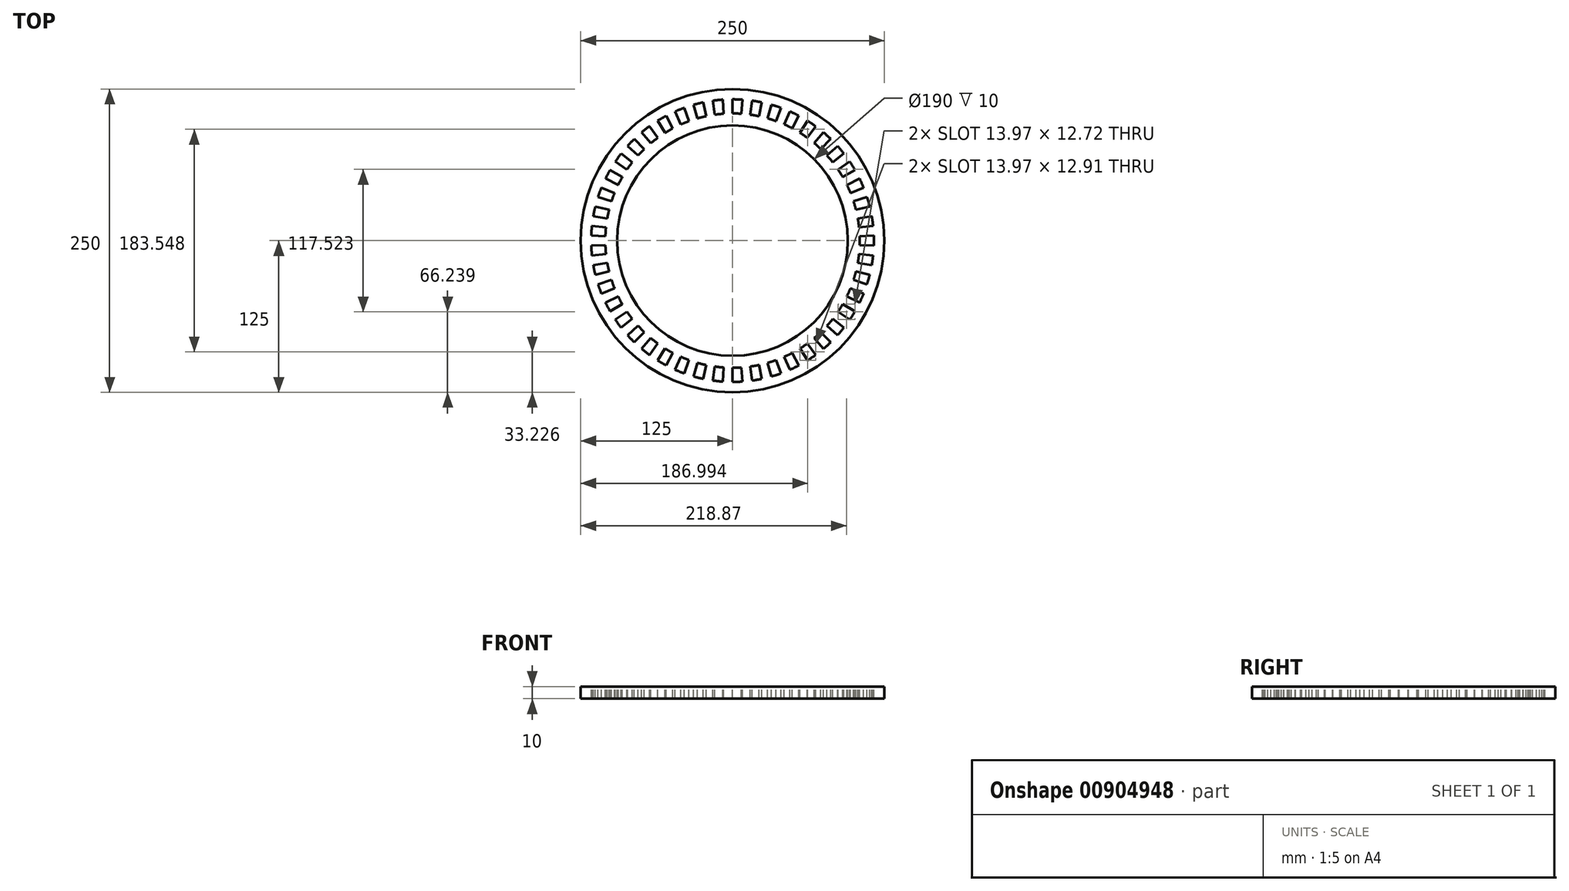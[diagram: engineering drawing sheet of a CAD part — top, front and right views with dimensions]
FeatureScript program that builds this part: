
annotation { "Feature Type Name" : "Feature", "Feature Type Description" : "" }
export const myFeature = defineFeature(function(context is Context, id is Id, definition is map)
    precondition{}
    {
        {
            var Q0;
            Q0=qCreatedBy(makeId("Top.planeOp"),FACE);
            var sketch = newSketch(context, id + "F0", { "sketchPlane" : qUnion([Q0])});
            skCircle(sketch, "E0", {"center": v(0, 0) * mm, "radius": 145 * mm});
            skArc(sketch, "E1", {"start": v(9.54, 136.41) * mm, "mid": v(4.77, 136.66) * mm, "end": v(0, 136.75) * mm});
            skArc(sketch, "E2", {"start": v(8, 114.55) * mm, "mid": v(4, 114.76) * mm, "end": v(0, 114.83) * mm});
            skLineSegment(sketch, "E3", {"start": v(0, 0) * mm, "end": v(0, 38.61) * mm, "construction": true});
            skLineSegment(sketch, "E4", {"start": v(0, 38.61) * mm, "end": v(0, 0) * mm, "construction": true});
            skLineSegment(sketch, "E5", {"start": v(0, 0) * mm, "end": v(-47.77, 0) * mm, "construction": true});
            skLineSegment(sketch, "E6", {"start": v(0, 30) * mm, "end": v(-10, 30) * mm});
            skLineSegment(sketch, "E7", {"start": v(-10, 30) * mm, "end": v(-10, 10) * mm});
            skLineSegment(sketch, "E8", {"start": v(-10, 10) * mm, "end": v(-30, 10) * mm});
            skLineSegment(sketch, "E9", {"start": v(-30, 10) * mm, "end": v(-30, 0) * mm});
            skLineSegment(sketch, "E10.MirrorCS", {"start": v(-30, -10) * mm, "end": v(-30, 0) * mm});
            skLineSegment(sketch, "E11.MirrorCS", {"start": v(-10, -10) * mm, "end": v(-30, -10) * mm});
            skLineSegment(sketch, "E12.MirrorCS", {"start": v(-10, -30) * mm, "end": v(-10, -10) * mm});
            skLineSegment(sketch, "E13.MirrorCS", {"start": v(0, -30) * mm, "end": v(-10, -30) * mm});
            skLineSegment(sketch, "E14.MirrorCS", {"start": v(0, 30) * mm, "end": v(10, 30) * mm});
            skLineSegment(sketch, "E15.MirrorCS", {"start": v(10, 30) * mm, "end": v(10, 10) * mm});
            skLineSegment(sketch, "E16.MirrorCS", {"start": v(10, 10) * mm, "end": v(30, 10) * mm});
            skLineSegment(sketch, "E17.MirrorCS", {"start": v(30, 10) * mm, "end": v(30, 0) * mm});
            skLineSegment(sketch, "E18.MirrorCS", {"start": v(30, -10) * mm, "end": v(30, 0) * mm});
            skLineSegment(sketch, "E19.MirrorCS", {"start": v(10, -10) * mm, "end": v(30, -10) * mm});
            skLineSegment(sketch, "E20.MirrorCS", {"start": v(0, -30) * mm, "end": v(10, -30) * mm});
            skLineSegment(sketch, "E21.MirrorCS", {"start": v(10, -30) * mm, "end": v(10, -10) * mm});
            skLineSegment(sketch, "E22", {"start": v(0, 114.83) * mm, "end": v(0, 136.75) * mm});
            skLineSegment(sketch, "E23", {"start": v(8, 114.55) * mm, "end": v(9.54, 136.41) * mm});
            skArc(sketch, "E24.1.0", {"start": v(-10, 114.4) * mm, "mid": v(-14, 113.98) * mm, "end": v(-17.96, 113.42) * mm});
            skLineSegment(sketch, "E24.1.1", {"start": v(-17.96, 113.42) * mm, "end": v(-21.4, 135.06) * mm});
            skArc(sketch, "E24.1.2", {"start": v(-11.92, 136.23) * mm, "mid": v(-16.67, 135.73) * mm, "end": v(-21.4, 135.06) * mm});
            skLineSegment(sketch, "E24.1.3", {"start": v(-10, 114.4) * mm, "end": v(-11.92, 136.23) * mm});
            skArc(sketch, "E24.2.0", {"start": v(-27.78, 111.42) * mm, "mid": v(-31.65, 110.39) * mm, "end": v(-35.49, 109.21) * mm});
            skLineSegment(sketch, "E24.2.1", {"start": v(-35.49, 109.21) * mm, "end": v(-42.26, 130.05) * mm});
            skArc(sketch, "E24.2.2", {"start": v(-33.08, 132.68) * mm, "mid": v(-37.7, 131.45) * mm, "end": v(-42.26, 130.05) * mm});
            skLineSegment(sketch, "E24.2.3", {"start": v(-27.78, 111.42) * mm, "end": v(-33.08, 132.68) * mm});
            skArc(sketch, "E24.3.0", {"start": v(-44.87, 105.7) * mm, "mid": v(-48.53, 104.07) * mm, "end": v(-52.13, 102.32) * mm});
            skLineSegment(sketch, "E24.3.1", {"start": v(-52.13, 102.32) * mm, "end": v(-62.08, 121.84) * mm});
            skArc(sketch, "E24.3.2", {"start": v(-53.43, 125.88) * mm, "mid": v(-57.8, 123.93) * mm, "end": v(-62.08, 121.84) * mm});
            skLineSegment(sketch, "E24.3.3", {"start": v(-44.87, 105.7) * mm, "end": v(-53.43, 125.88) * mm});
            skArc(sketch, "E24.4.0", {"start": v(-60.85, 97.38) * mm, "mid": v(-64.21, 95.2) * mm, "end": v(-67.5, 92.9) * mm});
            skLineSegment(sketch, "E24.4.1", {"start": v(-67.5, 92.9) * mm, "end": v(-80.38, 110.63) * mm});
            skArc(sketch, "E24.4.2", {"start": v(-72.47, 115.97) * mm, "mid": v(-76.47, 113.37) * mm, "end": v(-80.38, 110.63) * mm});
            skLineSegment(sketch, "E24.4.3", {"start": v(-60.85, 97.38) * mm, "end": v(-72.47, 115.97) * mm});
            skArc(sketch, "E24.5.0", {"start": v(-75.34, 86.67) * mm, "mid": v(-78.32, 83.98) * mm, "end": v(-81.2, 81.2) * mm});
            skLineSegment(sketch, "E24.5.1", {"start": v(-81.2, 81.2) * mm, "end": v(-96.7, 96.7) * mm});
            skArc(sketch, "E24.5.2", {"start": v(-89.71, 103.2) * mm, "mid": v(-93.26, 100.01) * mm, "end": v(-96.7, 96.7) * mm});
            skLineSegment(sketch, "E24.5.3", {"start": v(-75.34, 86.67) * mm, "end": v(-89.71, 103.2) * mm});
            skArc(sketch, "E24.6.0", {"start": v(-87.97, 73.81) * mm, "mid": v(-90.5, 70.7) * mm, "end": v(-92.9, 67.5) * mm});
            skLineSegment(sketch, "E24.6.1", {"start": v(-92.9, 67.5) * mm, "end": v(-110.63, 80.38) * mm});
            skArc(sketch, "E24.6.2", {"start": v(-104.75, 87.9) * mm, "mid": v(-107.76, 84.19) * mm, "end": v(-110.63, 80.38) * mm});
            skLineSegment(sketch, "E24.6.3", {"start": v(-87.97, 73.81) * mm, "end": v(-104.75, 87.9) * mm});
            skArc(sketch, "E24.7.0", {"start": v(-98.43, 59.14) * mm, "mid": v(-100.44, 55.67) * mm, "end": v(-102.32, 52.13) * mm});
            skLineSegment(sketch, "E24.7.1", {"start": v(-102.32, 52.13) * mm, "end": v(-121.84, 62.08) * mm});
            skArc(sketch, "E24.7.2", {"start": v(-117.22, 70.43) * mm, "mid": v(-119.6, 66.3) * mm, "end": v(-121.84, 62.08) * mm});
            skLineSegment(sketch, "E24.7.3", {"start": v(-98.43, 59.14) * mm, "end": v(-117.22, 70.43) * mm});
            skArc(sketch, "E24.8.0", {"start": v(-106.47, 43.02) * mm, "mid": v(-107.9, 39.28) * mm, "end": v(-109.21, 35.49) * mm});
            skLineSegment(sketch, "E24.8.1", {"start": v(-109.21, 35.49) * mm, "end": v(-130.05, 42.26) * mm});
            skArc(sketch, "E24.8.2", {"start": v(-126.79, 51.23) * mm, "mid": v(-128.5, 46.77) * mm, "end": v(-130.05, 42.26) * mm});
            skLineSegment(sketch, "E24.8.3", {"start": v(-106.47, 43.02) * mm, "end": v(-126.79, 51.23) * mm});
            skArc(sketch, "E24.9.0", {"start": v(-111.9, 25.83) * mm, "mid": v(-112.72, 21.91) * mm, "end": v(-113.42, 17.96) * mm});
            skLineSegment(sketch, "E24.9.1", {"start": v(-113.42, 17.96) * mm, "end": v(-135.06, 21.4) * mm});
            skArc(sketch, "E24.9.2", {"start": v(-133.24, 30.76) * mm, "mid": v(-134.23, 26.1) * mm, "end": v(-135.06, 21.4) * mm});
            skLineSegment(sketch, "E24.9.3", {"start": v(-111.9, 25.83) * mm, "end": v(-133.24, 30.76) * mm});
            skArc(sketch, "E24.10.0", {"start": v(-114.55, 8) * mm, "mid": v(-114.76, 4) * mm, "end": v(-114.83, 0) * mm});
            skLineSegment(sketch, "E24.10.1", {"start": v(-114.83, 0) * mm, "end": v(-136.75, 0) * mm});
            skArc(sketch, "E24.10.2", {"start": v(-136.41, 9.54) * mm, "mid": v(-136.66, 4.77) * mm, "end": v(-136.75, 0) * mm});
            skLineSegment(sketch, "E24.10.3", {"start": v(-114.55, 8) * mm, "end": v(-136.41, 9.54) * mm});
            skArc(sketch, "E24.11.0", {"start": v(-114.4, -10) * mm, "mid": v(-113.98, -14) * mm, "end": v(-113.42, -17.96) * mm});
            skLineSegment(sketch, "E24.11.1", {"start": v(-113.42, -17.96) * mm, "end": v(-135.06, -21.4) * mm});
            skArc(sketch, "E24.11.2", {"start": v(-136.23, -11.92) * mm, "mid": v(-135.73, -16.67) * mm, "end": v(-135.06, -21.4) * mm});
            skLineSegment(sketch, "E24.11.3", {"start": v(-114.4, -10) * mm, "end": v(-136.23, -11.92) * mm});
            skArc(sketch, "E24.12.0", {"start": v(-111.42, -27.78) * mm, "mid": v(-110.39, -31.65) * mm, "end": v(-109.21, -35.49) * mm});
            skLineSegment(sketch, "E24.12.1", {"start": v(-109.21, -35.49) * mm, "end": v(-130.05, -42.26) * mm});
            skArc(sketch, "E24.12.2", {"start": v(-132.68, -33.08) * mm, "mid": v(-131.45, -37.7) * mm, "end": v(-130.05, -42.26) * mm});
            skLineSegment(sketch, "E24.12.3", {"start": v(-111.42, -27.78) * mm, "end": v(-132.68, -33.08) * mm});
            skArc(sketch, "E24.13.0", {"start": v(-105.7, -44.87) * mm, "mid": v(-104.07, -48.53) * mm, "end": v(-102.32, -52.13) * mm});
            skLineSegment(sketch, "E24.13.1", {"start": v(-102.32, -52.13) * mm, "end": v(-121.84, -62.08) * mm});
            skArc(sketch, "E24.13.2", {"start": v(-125.88, -53.43) * mm, "mid": v(-123.93, -57.8) * mm, "end": v(-121.84, -62.08) * mm});
            skLineSegment(sketch, "E24.13.3", {"start": v(-105.7, -44.87) * mm, "end": v(-125.88, -53.43) * mm});
            skArc(sketch, "E24.14.0", {"start": v(-97.38, -60.85) * mm, "mid": v(-95.2, -64.21) * mm, "end": v(-92.9, -67.5) * mm});
            skLineSegment(sketch, "E24.14.1", {"start": v(-92.9, -67.5) * mm, "end": v(-110.63, -80.38) * mm});
            skArc(sketch, "E24.14.2", {"start": v(-115.97, -72.47) * mm, "mid": v(-113.37, -76.47) * mm, "end": v(-110.63, -80.38) * mm});
            skLineSegment(sketch, "E24.14.3", {"start": v(-97.38, -60.85) * mm, "end": v(-115.97, -72.47) * mm});
            skArc(sketch, "E24.15.0", {"start": v(-86.67, -75.34) * mm, "mid": v(-83.98, -78.32) * mm, "end": v(-81.2, -81.2) * mm});
            skLineSegment(sketch, "E24.15.1", {"start": v(-81.2, -81.2) * mm, "end": v(-96.7, -96.7) * mm});
            skArc(sketch, "E24.15.2", {"start": v(-103.2, -89.71) * mm, "mid": v(-100.01, -93.26) * mm, "end": v(-96.7, -96.7) * mm});
            skLineSegment(sketch, "E24.15.3", {"start": v(-86.67, -75.34) * mm, "end": v(-103.2, -89.71) * mm});
            skArc(sketch, "E24.16.0", {"start": v(-73.81, -87.97) * mm, "mid": v(-70.7, -90.5) * mm, "end": v(-67.5, -92.9) * mm});
            skLineSegment(sketch, "E24.16.1", {"start": v(-67.5, -92.9) * mm, "end": v(-80.38, -110.63) * mm});
            skArc(sketch, "E24.16.2", {"start": v(-87.9, -104.75) * mm, "mid": v(-84.19, -107.76) * mm, "end": v(-80.38, -110.63) * mm});
            skLineSegment(sketch, "E24.16.3", {"start": v(-73.81, -87.97) * mm, "end": v(-87.9, -104.75) * mm});
            skArc(sketch, "E24.17.0", {"start": v(-59.14, -98.43) * mm, "mid": v(-55.67, -100.44) * mm, "end": v(-52.13, -102.32) * mm});
            skLineSegment(sketch, "E24.17.1", {"start": v(-52.13, -102.32) * mm, "end": v(-62.08, -121.84) * mm});
            skArc(sketch, "E24.17.2", {"start": v(-70.43, -117.22) * mm, "mid": v(-66.3, -119.6) * mm, "end": v(-62.08, -121.84) * mm});
            skLineSegment(sketch, "E24.17.3", {"start": v(-59.14, -98.43) * mm, "end": v(-70.43, -117.22) * mm});
            skArc(sketch, "E24.18.0", {"start": v(-43.02, -106.47) * mm, "mid": v(-39.28, -107.9) * mm, "end": v(-35.49, -109.21) * mm});
            skLineSegment(sketch, "E24.18.1", {"start": v(-35.49, -109.21) * mm, "end": v(-42.26, -130.05) * mm});
            skArc(sketch, "E24.18.2", {"start": v(-51.23, -126.79) * mm, "mid": v(-46.77, -128.5) * mm, "end": v(-42.26, -130.05) * mm});
            skLineSegment(sketch, "E24.18.3", {"start": v(-43.02, -106.47) * mm, "end": v(-51.23, -126.79) * mm});
            skArc(sketch, "E24.19.0", {"start": v(-25.83, -111.9) * mm, "mid": v(-21.91, -112.72) * mm, "end": v(-17.96, -113.42) * mm});
            skLineSegment(sketch, "E24.19.1", {"start": v(-17.96, -113.42) * mm, "end": v(-21.4, -135.06) * mm});
            skArc(sketch, "E24.19.2", {"start": v(-30.76, -133.24) * mm, "mid": v(-26.1, -134.23) * mm, "end": v(-21.4, -135.06) * mm});
            skLineSegment(sketch, "E24.19.3", {"start": v(-25.83, -111.9) * mm, "end": v(-30.76, -133.24) * mm});
            skArc(sketch, "E24.20.0", {"start": v(-8, -114.55) * mm, "mid": v(-4, -114.76) * mm, "end": v(0, -114.83) * mm});
            skLineSegment(sketch, "E24.20.1", {"start": v(0, -114.83) * mm, "end": v(0, -136.75) * mm});
            skArc(sketch, "E24.20.2", {"start": v(-9.54, -136.41) * mm, "mid": v(-4.77, -136.66) * mm, "end": v(0, -136.75) * mm});
            skLineSegment(sketch, "E24.20.3", {"start": v(-8, -114.55) * mm, "end": v(-9.54, -136.41) * mm});
            skArc(sketch, "E24.21.0", {"start": v(10, -114.4) * mm, "mid": v(14, -113.98) * mm, "end": v(17.96, -113.42) * mm});
            skLineSegment(sketch, "E24.21.1", {"start": v(17.96, -113.42) * mm, "end": v(21.4, -135.06) * mm});
            skArc(sketch, "E24.21.2", {"start": v(11.92, -136.23) * mm, "mid": v(16.67, -135.73) * mm, "end": v(21.4, -135.06) * mm});
            skLineSegment(sketch, "E24.21.3", {"start": v(10, -114.4) * mm, "end": v(11.92, -136.23) * mm});
            skArc(sketch, "E24.22.0", {"start": v(27.78, -111.42) * mm, "mid": v(31.65, -110.39) * mm, "end": v(35.49, -109.21) * mm});
            skLineSegment(sketch, "E24.22.1", {"start": v(35.49, -109.21) * mm, "end": v(42.26, -130.05) * mm});
            skArc(sketch, "E24.22.2", {"start": v(33.08, -132.68) * mm, "mid": v(37.7, -131.45) * mm, "end": v(42.26, -130.05) * mm});
            skLineSegment(sketch, "E24.22.3", {"start": v(27.78, -111.42) * mm, "end": v(33.08, -132.68) * mm});
            skArc(sketch, "E24.23.0", {"start": v(44.87, -105.7) * mm, "mid": v(48.53, -104.07) * mm, "end": v(52.13, -102.32) * mm});
            skLineSegment(sketch, "E24.23.1", {"start": v(52.13, -102.32) * mm, "end": v(62.08, -121.84) * mm});
            skArc(sketch, "E24.23.2", {"start": v(53.43, -125.88) * mm, "mid": v(57.8, -123.93) * mm, "end": v(62.08, -121.84) * mm});
            skLineSegment(sketch, "E24.23.3", {"start": v(44.87, -105.7) * mm, "end": v(53.43, -125.88) * mm});
            skArc(sketch, "E24.24.0", {"start": v(60.85, -97.38) * mm, "mid": v(64.21, -95.2) * mm, "end": v(67.5, -92.9) * mm});
            skLineSegment(sketch, "E24.24.1", {"start": v(67.5, -92.9) * mm, "end": v(80.38, -110.63) * mm});
            skArc(sketch, "E24.24.2", {"start": v(72.47, -115.97) * mm, "mid": v(76.47, -113.37) * mm, "end": v(80.38, -110.63) * mm});
            skLineSegment(sketch, "E24.24.3", {"start": v(60.85, -97.38) * mm, "end": v(72.47, -115.97) * mm});
            skArc(sketch, "E24.25.0", {"start": v(75.34, -86.67) * mm, "mid": v(78.32, -83.98) * mm, "end": v(81.2, -81.2) * mm});
            skLineSegment(sketch, "E24.25.1", {"start": v(81.2, -81.2) * mm, "end": v(96.7, -96.7) * mm});
            skArc(sketch, "E24.25.2", {"start": v(89.71, -103.2) * mm, "mid": v(93.26, -100.01) * mm, "end": v(96.7, -96.7) * mm});
            skLineSegment(sketch, "E24.25.3", {"start": v(75.34, -86.67) * mm, "end": v(89.71, -103.2) * mm});
            skArc(sketch, "E24.26.0", {"start": v(87.97, -73.81) * mm, "mid": v(90.5, -70.7) * mm, "end": v(92.9, -67.5) * mm});
            skLineSegment(sketch, "E24.26.1", {"start": v(92.9, -67.5) * mm, "end": v(110.63, -80.38) * mm});
            skArc(sketch, "E24.26.2", {"start": v(104.75, -87.9) * mm, "mid": v(107.76, -84.19) * mm, "end": v(110.63, -80.38) * mm});
            skLineSegment(sketch, "E24.26.3", {"start": v(87.97, -73.81) * mm, "end": v(104.75, -87.9) * mm});
            skArc(sketch, "E24.27.0", {"start": v(98.43, -59.14) * mm, "mid": v(100.44, -55.67) * mm, "end": v(102.32, -52.13) * mm});
            skLineSegment(sketch, "E24.27.1", {"start": v(102.32, -52.13) * mm, "end": v(121.84, -62.08) * mm});
            skArc(sketch, "E24.27.2", {"start": v(117.22, -70.43) * mm, "mid": v(119.6, -66.3) * mm, "end": v(121.84, -62.08) * mm});
            skLineSegment(sketch, "E24.27.3", {"start": v(98.43, -59.14) * mm, "end": v(117.22, -70.43) * mm});
            skArc(sketch, "E24.28.0", {"start": v(106.47, -43.02) * mm, "mid": v(107.9, -39.28) * mm, "end": v(109.21, -35.49) * mm});
            skLineSegment(sketch, "E24.28.1", {"start": v(109.21, -35.49) * mm, "end": v(130.05, -42.26) * mm});
            skArc(sketch, "E24.28.2", {"start": v(126.79, -51.23) * mm, "mid": v(128.5, -46.77) * mm, "end": v(130.05, -42.26) * mm});
            skLineSegment(sketch, "E24.28.3", {"start": v(106.47, -43.02) * mm, "end": v(126.79, -51.23) * mm});
            skArc(sketch, "E24.29.0", {"start": v(111.9, -25.83) * mm, "mid": v(112.72, -21.91) * mm, "end": v(113.42, -17.96) * mm});
            skLineSegment(sketch, "E24.29.1", {"start": v(113.42, -17.96) * mm, "end": v(135.06, -21.4) * mm});
            skArc(sketch, "E24.29.2", {"start": v(133.24, -30.76) * mm, "mid": v(134.23, -26.1) * mm, "end": v(135.06, -21.4) * mm});
            skLineSegment(sketch, "E24.29.3", {"start": v(111.9, -25.83) * mm, "end": v(133.24, -30.76) * mm});
            skArc(sketch, "E24.30.0", {"start": v(114.55, -8) * mm, "mid": v(114.76, -4) * mm, "end": v(114.83, 0) * mm});
            skLineSegment(sketch, "E24.30.1", {"start": v(114.83, 0) * mm, "end": v(136.75, 0) * mm});
            skArc(sketch, "E24.30.2", {"start": v(136.41, -9.54) * mm, "mid": v(136.66, -4.77) * mm, "end": v(136.75, 0) * mm});
            skLineSegment(sketch, "E24.30.3", {"start": v(114.55, -8) * mm, "end": v(136.41, -9.54) * mm});
            skArc(sketch, "E24.31.0", {"start": v(114.4, 10) * mm, "mid": v(113.98, 14) * mm, "end": v(113.42, 17.96) * mm});
            skLineSegment(sketch, "E24.31.1", {"start": v(113.42, 17.96) * mm, "end": v(135.06, 21.4) * mm});
            skArc(sketch, "E24.31.2", {"start": v(136.23, 11.92) * mm, "mid": v(135.73, 16.67) * mm, "end": v(135.06, 21.4) * mm});
            skLineSegment(sketch, "E24.31.3", {"start": v(114.4, 10) * mm, "end": v(136.23, 11.92) * mm});
            skArc(sketch, "E24.32.0", {"start": v(111.42, 27.78) * mm, "mid": v(110.39, 31.65) * mm, "end": v(109.21, 35.49) * mm});
            skLineSegment(sketch, "E24.32.1", {"start": v(109.21, 35.49) * mm, "end": v(130.05, 42.26) * mm});
            skArc(sketch, "E24.32.2", {"start": v(132.68, 33.08) * mm, "mid": v(131.45, 37.7) * mm, "end": v(130.05, 42.26) * mm});
            skLineSegment(sketch, "E24.32.3", {"start": v(111.42, 27.78) * mm, "end": v(132.68, 33.08) * mm});
            skArc(sketch, "E24.33.0", {"start": v(105.7, 44.87) * mm, "mid": v(104.07, 48.53) * mm, "end": v(102.32, 52.13) * mm});
            skLineSegment(sketch, "E24.33.1", {"start": v(102.32, 52.13) * mm, "end": v(121.84, 62.08) * mm});
            skArc(sketch, "E24.33.2", {"start": v(125.88, 53.43) * mm, "mid": v(123.93, 57.8) * mm, "end": v(121.84, 62.08) * mm});
            skLineSegment(sketch, "E24.33.3", {"start": v(105.7, 44.87) * mm, "end": v(125.88, 53.43) * mm});
            skArc(sketch, "E24.34.0", {"start": v(97.38, 60.85) * mm, "mid": v(95.2, 64.21) * mm, "end": v(92.9, 67.5) * mm});
            skLineSegment(sketch, "E24.34.1", {"start": v(92.9, 67.5) * mm, "end": v(110.63, 80.38) * mm});
            skArc(sketch, "E24.34.2", {"start": v(115.97, 72.47) * mm, "mid": v(113.37, 76.47) * mm, "end": v(110.63, 80.38) * mm});
            skLineSegment(sketch, "E24.34.3", {"start": v(97.38, 60.85) * mm, "end": v(115.97, 72.47) * mm});
            skArc(sketch, "E24.35.0", {"start": v(86.67, 75.34) * mm, "mid": v(83.98, 78.32) * mm, "end": v(81.2, 81.2) * mm});
            skLineSegment(sketch, "E24.35.1", {"start": v(81.2, 81.2) * mm, "end": v(96.7, 96.7) * mm});
            skArc(sketch, "E24.35.2", {"start": v(103.2, 89.71) * mm, "mid": v(100.01, 93.26) * mm, "end": v(96.7, 96.7) * mm});
            skLineSegment(sketch, "E24.35.3", {"start": v(86.67, 75.34) * mm, "end": v(103.2, 89.71) * mm});
            skArc(sketch, "E24.36.0", {"start": v(73.81, 87.97) * mm, "mid": v(70.7, 90.5) * mm, "end": v(67.5, 92.9) * mm});
            skLineSegment(sketch, "E24.36.1", {"start": v(67.5, 92.9) * mm, "end": v(80.38, 110.63) * mm});
            skArc(sketch, "E24.36.2", {"start": v(87.9, 104.75) * mm, "mid": v(84.19, 107.76) * mm, "end": v(80.38, 110.63) * mm});
            skLineSegment(sketch, "E24.36.3", {"start": v(73.81, 87.97) * mm, "end": v(87.9, 104.75) * mm});
            skArc(sketch, "E24.37.0", {"start": v(59.14, 98.43) * mm, "mid": v(55.67, 100.44) * mm, "end": v(52.13, 102.32) * mm});
            skLineSegment(sketch, "E24.37.1", {"start": v(52.13, 102.32) * mm, "end": v(62.08, 121.84) * mm});
            skArc(sketch, "E24.37.2", {"start": v(70.43, 117.22) * mm, "mid": v(66.3, 119.6) * mm, "end": v(62.08, 121.84) * mm});
            skLineSegment(sketch, "E24.37.3", {"start": v(59.14, 98.43) * mm, "end": v(70.43, 117.22) * mm});
            skArc(sketch, "E24.38.0", {"start": v(43.02, 106.47) * mm, "mid": v(39.28, 107.9) * mm, "end": v(35.49, 109.21) * mm});
            skLineSegment(sketch, "E24.38.1", {"start": v(35.49, 109.21) * mm, "end": v(42.26, 130.05) * mm});
            skArc(sketch, "E24.38.2", {"start": v(51.23, 126.79) * mm, "mid": v(46.77, 128.5) * mm, "end": v(42.26, 130.05) * mm});
            skLineSegment(sketch, "E24.38.3", {"start": v(43.02, 106.47) * mm, "end": v(51.23, 126.79) * mm});
            skArc(sketch, "E24.39.0", {"start": v(25.83, 111.9) * mm, "mid": v(21.91, 112.72) * mm, "end": v(17.96, 113.42) * mm});
            skLineSegment(sketch, "E24.39.1", {"start": v(17.96, 113.42) * mm, "end": v(21.4, 135.06) * mm});
            skArc(sketch, "E24.39.2", {"start": v(30.76, 133.24) * mm, "mid": v(26.1, 134.23) * mm, "end": v(21.4, 135.06) * mm});
            skLineSegment(sketch, "E24.39.3", {"start": v(25.83, 111.9) * mm, "end": v(30.76, 133.24) * mm});
            skCircle(sketch, "E25", {"center": v(0, 0) * mm, "radius": 50 * mm});
            skSolve(sketch);
        }
        {
            var Q0;
            Q0=makeQuery(id+"F0.imprint","IMPRINT",FACE,{"disambiguationData":[TD([[makeQuery(id+"F0.imprint","IMPRINT",EDGE,{"derivedFrom":sQuery(id+"F0.wireOp",EDGE,"E6")}),-1.0]])]});
            extrude(context, id + "F1", {"entities" : qUnion([Q0]), "depth" : 5 * mm, "offsetDistance" : 25 * mm});
        }
        {
            var Q0;
            Q0=makeQuery(id+"F1.opExtrude","CAP_FACE",FACE,{"disambiguationData":[OSD([sQuery(id+"F0.wireOp",EDGE,"E6"),sQuery(id+"F0.wireOp",EDGE,"E7"),sQuery(id+"F0.wireOp",EDGE,"E8"),sQuery(id+"F0.wireOp",EDGE,"E9"),sQuery(id+"F0.wireOp",EDGE,"E10.MirrorCS"),sQuery(id+"F0.wireOp",EDGE,"E11.MirrorCS"),sQuery(id+"F0.wireOp",EDGE,"E12.MirrorCS"),sQuery(id+"F0.wireOp",EDGE,"E13.MirrorCS"),sQuery(id+"F0.wireOp",EDGE,"E14.MirrorCS"),sQuery(id+"F0.wireOp",EDGE,"E15.MirrorCS"),sQuery(id+"F0.wireOp",EDGE,"E16.MirrorCS"),sQuery(id+"F0.wireOp",EDGE,"E17.MirrorCS"),sQuery(id+"F0.wireOp",EDGE,"E18.MirrorCS"),sQuery(id+"F0.wireOp",EDGE,"E19.MirrorCS"),sQuery(id+"F0.wireOp",EDGE,"E20.MirrorCS"),sQuery(id+"F0.wireOp",EDGE,"E21.MirrorCS"),sQuery(id+"F0.wireOp",EDGE,"E25")])],"isStart":false});
            var sketch = newSketch(context, id + "F2", { "sketchPlane" : qUnion([Q0])});
            skCircle(sketch, "E26", {"center": v(0, 0) * mm, "radius": 125 * mm});
            skCircle(sketch, "E27", {"center": v(0, 0) * mm, "radius": 40.45 * mm});
            skSolve(sketch);
        }
        {
            var Q0;
            Q0=qSketchRegion(id+"F2",true);
            extrude(context, id + "F3", {"entities" : qUnion([Q0]), "operationType" : NewBodyOperationType.ADD, "oppositeDirection" : true, "depth" : 10 * mm, "offsetDistance" : 25 * mm});
        }
        {
            var Q0;
            Q0=makeQuery(id+"F3.boolean.opBoolean","MERGE",FACE,{"derivedFrom":[makeQuery(id+"F1.opExtrude","CAP_FACE",FACE,{"disambiguationData":[OSD([sQuery(id+"F0.wireOp",EDGE,"E6"),sQuery(id+"F0.wireOp",EDGE,"E7"),sQuery(id+"F0.wireOp",EDGE,"E8"),sQuery(id+"F0.wireOp",EDGE,"E9"),sQuery(id+"F0.wireOp",EDGE,"E10.MirrorCS"),sQuery(id+"F0.wireOp",EDGE,"E11.MirrorCS"),sQuery(id+"F0.wireOp",EDGE,"E12.MirrorCS"),sQuery(id+"F0.wireOp",EDGE,"E13.MirrorCS"),sQuery(id+"F0.wireOp",EDGE,"E14.MirrorCS"),sQuery(id+"F0.wireOp",EDGE,"E15.MirrorCS"),sQuery(id+"F0.wireOp",EDGE,"E16.MirrorCS"),sQuery(id+"F0.wireOp",EDGE,"E17.MirrorCS"),sQuery(id+"F0.wireOp",EDGE,"E18.MirrorCS"),sQuery(id+"F0.wireOp",EDGE,"E19.MirrorCS"),sQuery(id+"F0.wireOp",EDGE,"E20.MirrorCS"),sQuery(id+"F0.wireOp",EDGE,"E21.MirrorCS"),sQuery(id+"F0.wireOp",EDGE,"E25")])],"isStart":false}),makeQuery(id+"F3.opExtrude","CAP_FACE",FACE,{"disambiguationData":[OSD([sQuery(id+"F2.wireOp",EDGE,"E26"),sQuery(id+"F2.wireOp",EDGE,"E27")])],"isStart":true})]});
            var sketch = newSketch(context, id + "F4", { "sketchPlane" : qUnion([Q0])});
            skLineSegment(sketch, "E28", {"start": v(0, 104.8) * mm, "end": v(0, 116.46) * mm});
            skLineSegment(sketch, "E29", {"start": v(0, 116.46) * mm, "end": v(0, 104.8) * mm});
            skLineSegment(sketch, "E30", {"start": v(7.31, 104.55) * mm, "end": v(8.12, 116.17) * mm});
            skArc(sketch, "E31", {"start": v(8.12, 116.17) * mm, "mid": v(4.06, 116.39) * mm, "end": v(0, 116.46) * mm});
            skArc(sketch, "E32", {"start": v(7.31, 104.55) * mm, "mid": v(3.66, 104.74) * mm, "end": v(0, 104.8) * mm});
            skArc(sketch, "E33.1.0", {"start": v(-7.31, 104.55) * mm, "mid": v(-10.95, 104.23) * mm, "end": v(-14.59, 103.78) * mm});
            skLineSegment(sketch, "E33.1.1", {"start": v(-16.2, 115.32) * mm, "end": v(-14.59, 103.78) * mm});
            skArc(sketch, "E33.1.2", {"start": v(-8.12, 116.17) * mm, "mid": v(-12.17, 115.82) * mm, "end": v(-16.2, 115.32) * mm});
            skLineSegment(sketch, "E33.1.3", {"start": v(-7.31, 104.55) * mm, "end": v(-8.12, 116.17) * mm});
            skArc(sketch, "E33.2.0", {"start": v(-21.79, 102.51) * mm, "mid": v(-25.35, 101.69) * mm, "end": v(-28.89, 100.74) * mm});
            skLineSegment(sketch, "E33.2.1", {"start": v(-32.1, 111.95) * mm, "end": v(-28.89, 100.74) * mm});
            skArc(sketch, "E33.2.2", {"start": v(-24.21, 113.91) * mm, "mid": v(-28.17, 113) * mm, "end": v(-32.1, 111.95) * mm});
            skLineSegment(sketch, "E33.2.3", {"start": v(-21.79, 102.51) * mm, "end": v(-24.21, 113.91) * mm});
            skArc(sketch, "E33.3.0", {"start": v(-35.84, 98.48) * mm, "mid": v(-39.26, 97.17) * mm, "end": v(-42.63, 95.74) * mm});
            skLineSegment(sketch, "E33.3.1", {"start": v(-47.37, 106.39) * mm, "end": v(-42.63, 95.74) * mm});
            skArc(sketch, "E33.3.2", {"start": v(-39.83, 109.43) * mm, "mid": v(-43.63, 107.98) * mm, "end": v(-47.37, 106.39) * mm});
            skLineSegment(sketch, "E33.3.3", {"start": v(-35.84, 98.48) * mm, "end": v(-39.83, 109.43) * mm});
            skArc(sketch, "E33.4.0", {"start": v(-49.2, 92.54) * mm, "mid": v(-52.4, 90.76) * mm, "end": v(-55.54, 88.88) * mm});
            skLineSegment(sketch, "E33.4.1", {"start": v(-61.71, 98.76) * mm, "end": v(-55.54, 88.88) * mm});
            skArc(sketch, "E33.4.2", {"start": v(-54.67, 102.82) * mm, "mid": v(-58.23, 100.85) * mm, "end": v(-61.71, 98.76) * mm});
            skLineSegment(sketch, "E33.4.3", {"start": v(-49.2, 92.54) * mm, "end": v(-54.67, 102.82) * mm});
            skArc(sketch, "E33.5.0", {"start": v(-61.6, 84.79) * mm, "mid": v(-64.52, 82.59) * mm, "end": v(-67.37, 80.28) * mm});
            skLineSegment(sketch, "E33.5.1", {"start": v(-74.86, 89.21) * mm, "end": v(-67.37, 80.28) * mm});
            skArc(sketch, "E33.5.2", {"start": v(-68.45, 94.22) * mm, "mid": v(-71.7, 91.77) * mm, "end": v(-74.86, 89.21) * mm});
            skLineSegment(sketch, "E33.5.3", {"start": v(-61.6, 84.79) * mm, "end": v(-68.45, 94.22) * mm});
            skArc(sketch, "E33.6.0", {"start": v(-72.8, 75.39) * mm, "mid": v(-75.39, 72.8) * mm, "end": v(-77.88, 70.13) * mm});
            skLineSegment(sketch, "E33.6.1", {"start": v(-86.54, 77.92) * mm, "end": v(-77.88, 70.13) * mm});
            skArc(sketch, "E33.6.2", {"start": v(-80.9, 83.77) * mm, "mid": v(-83.77, 80.9) * mm, "end": v(-86.54, 77.92) * mm});
            skLineSegment(sketch, "E33.6.3", {"start": v(-72.8, 75.39) * mm, "end": v(-80.9, 83.77) * mm});
            skArc(sketch, "E33.7.0", {"start": v(-82.59, 64.52) * mm, "mid": v(-84.79, 61.6) * mm, "end": v(-86.89, 58.6) * mm});
            skLineSegment(sketch, "E33.7.1", {"start": v(-96.55, 65.12) * mm, "end": v(-86.89, 58.6) * mm});
            skArc(sketch, "E33.7.2", {"start": v(-91.77, 71.7) * mm, "mid": v(-94.22, 68.45) * mm, "end": v(-96.55, 65.12) * mm});
            skLineSegment(sketch, "E33.7.3", {"start": v(-82.59, 64.52) * mm, "end": v(-91.77, 71.7) * mm});
            skArc(sketch, "E33.8.0", {"start": v(-90.76, 52.4) * mm, "mid": v(-92.54, 49.2) * mm, "end": v(-94.2, 45.94) * mm});
            skLineSegment(sketch, "E33.8.1", {"start": v(-104.67, 51.05) * mm, "end": v(-94.2, 45.94) * mm});
            skArc(sketch, "E33.8.2", {"start": v(-100.85, 58.23) * mm, "mid": v(-102.82, 54.67) * mm, "end": v(-104.67, 51.05) * mm});
            skLineSegment(sketch, "E33.8.3", {"start": v(-90.76, 52.4) * mm, "end": v(-100.85, 58.23) * mm});
            skArc(sketch, "E33.9.0", {"start": v(-97.17, 39.26) * mm, "mid": v(-98.48, 35.84) * mm, "end": v(-99.67, 32.39) * mm});
            skLineSegment(sketch, "E33.9.1", {"start": v(-110.76, 35.99) * mm, "end": v(-99.67, 32.39) * mm});
            skArc(sketch, "E33.9.2", {"start": v(-107.98, 43.63) * mm, "mid": v(-109.43, 39.83) * mm, "end": v(-110.76, 35.99) * mm});
            skLineSegment(sketch, "E33.9.3", {"start": v(-97.17, 39.26) * mm, "end": v(-107.98, 43.63) * mm});
            skArc(sketch, "E33.10.0", {"start": v(-101.69, 25.35) * mm, "mid": v(-102.51, 21.79) * mm, "end": v(-103.21, 18.2) * mm});
            skLineSegment(sketch, "E33.10.1", {"start": v(-114.69, 20.22) * mm, "end": v(-103.21, 18.2) * mm});
            skArc(sketch, "E33.10.2", {"start": v(-113, 28.17) * mm, "mid": v(-113.91, 24.21) * mm, "end": v(-114.69, 20.22) * mm});
            skLineSegment(sketch, "E33.10.3", {"start": v(-101.69, 25.35) * mm, "end": v(-113, 28.17) * mm});
            skArc(sketch, "E33.11.0", {"start": v(-104.23, 10.95) * mm, "mid": v(-104.55, 7.31) * mm, "end": v(-104.74, 3.66) * mm});
            skLineSegment(sketch, "E33.11.1", {"start": v(-116.39, 4.06) * mm, "end": v(-104.74, 3.66) * mm});
            skArc(sketch, "E33.11.2", {"start": v(-115.82, 12.17) * mm, "mid": v(-116.17, 8.12) * mm, "end": v(-116.39, 4.06) * mm});
            skLineSegment(sketch, "E33.11.3", {"start": v(-104.23, 10.95) * mm, "end": v(-115.82, 12.17) * mm});
            skArc(sketch, "E33.12.0", {"start": v(-104.74, -3.66) * mm, "mid": v(-104.55, -7.31) * mm, "end": v(-104.23, -10.95) * mm});
            skLineSegment(sketch, "E33.12.1", {"start": v(-115.82, -12.17) * mm, "end": v(-104.23, -10.95) * mm});
            skArc(sketch, "E33.12.2", {"start": v(-116.39, -4.06) * mm, "mid": v(-116.17, -8.12) * mm, "end": v(-115.82, -12.17) * mm});
            skLineSegment(sketch, "E33.12.3", {"start": v(-104.74, -3.66) * mm, "end": v(-116.39, -4.06) * mm});
            skArc(sketch, "E33.13.0", {"start": v(-103.21, -18.2) * mm, "mid": v(-102.51, -21.79) * mm, "end": v(-101.69, -25.35) * mm});
            skLineSegment(sketch, "E33.13.1", {"start": v(-113, -28.17) * mm, "end": v(-101.69, -25.35) * mm});
            skArc(sketch, "E33.13.2", {"start": v(-114.69, -20.22) * mm, "mid": v(-113.91, -24.21) * mm, "end": v(-113, -28.17) * mm});
            skLineSegment(sketch, "E33.13.3", {"start": v(-103.21, -18.2) * mm, "end": v(-114.69, -20.22) * mm});
            skArc(sketch, "E33.14.0", {"start": v(-99.67, -32.39) * mm, "mid": v(-98.48, -35.84) * mm, "end": v(-97.17, -39.26) * mm});
            skLineSegment(sketch, "E33.14.1", {"start": v(-107.98, -43.63) * mm, "end": v(-97.17, -39.26) * mm});
            skArc(sketch, "E33.14.2", {"start": v(-110.76, -35.99) * mm, "mid": v(-109.43, -39.83) * mm, "end": v(-107.98, -43.63) * mm});
            skLineSegment(sketch, "E33.14.3", {"start": v(-99.67, -32.39) * mm, "end": v(-110.76, -35.99) * mm});
            skArc(sketch, "E33.15.0", {"start": v(-94.2, -45.94) * mm, "mid": v(-92.54, -49.2) * mm, "end": v(-90.76, -52.4) * mm});
            skLineSegment(sketch, "E33.15.1", {"start": v(-100.85, -58.23) * mm, "end": v(-90.76, -52.4) * mm});
            skArc(sketch, "E33.15.2", {"start": v(-104.67, -51.05) * mm, "mid": v(-102.82, -54.67) * mm, "end": v(-100.85, -58.23) * mm});
            skLineSegment(sketch, "E33.15.3", {"start": v(-94.2, -45.94) * mm, "end": v(-104.67, -51.05) * mm});
            skArc(sketch, "E33.16.0", {"start": v(-86.89, -58.6) * mm, "mid": v(-84.79, -61.6) * mm, "end": v(-82.59, -64.52) * mm});
            skLineSegment(sketch, "E33.16.1", {"start": v(-91.77, -71.7) * mm, "end": v(-82.59, -64.52) * mm});
            skArc(sketch, "E33.16.2", {"start": v(-96.55, -65.12) * mm, "mid": v(-94.22, -68.45) * mm, "end": v(-91.77, -71.7) * mm});
            skLineSegment(sketch, "E33.16.3", {"start": v(-86.89, -58.6) * mm, "end": v(-96.55, -65.12) * mm});
            skArc(sketch, "E33.17.0", {"start": v(-77.88, -70.13) * mm, "mid": v(-75.39, -72.8) * mm, "end": v(-72.8, -75.39) * mm});
            skLineSegment(sketch, "E33.17.1", {"start": v(-80.9, -83.77) * mm, "end": v(-72.8, -75.39) * mm});
            skArc(sketch, "E33.17.2", {"start": v(-86.54, -77.92) * mm, "mid": v(-83.77, -80.9) * mm, "end": v(-80.9, -83.77) * mm});
            skLineSegment(sketch, "E33.17.3", {"start": v(-77.88, -70.13) * mm, "end": v(-86.54, -77.92) * mm});
            skArc(sketch, "E34.3.18.0", {"start": v(-67.37, -80.28) * mm, "mid": v(-64.52, -82.59) * mm, "end": v(-61.6, -84.79) * mm});
            skLineSegment(sketch, "E34.4.18.0", {"start": v(-68.45, -94.22) * mm, "end": v(-61.6, -84.79) * mm});
            skArc(sketch, "E34.7.18.0", {"start": v(-74.86, -89.21) * mm, "mid": v(-71.7, -91.77) * mm, "end": v(-68.45, -94.22) * mm});
            skLineSegment(sketch, "E34.11.18.0", {"start": v(-67.37, -80.28) * mm, "end": v(-74.86, -89.21) * mm});
            skArc(sketch, "E34.3.19.0", {"start": v(-55.54, -88.88) * mm, "mid": v(-52.4, -90.76) * mm, "end": v(-49.2, -92.54) * mm});
            skLineSegment(sketch, "E34.4.19.0", {"start": v(-54.67, -102.82) * mm, "end": v(-49.2, -92.54) * mm});
            skArc(sketch, "E34.7.19.0", {"start": v(-61.71, -98.76) * mm, "mid": v(-58.23, -100.85) * mm, "end": v(-54.67, -102.82) * mm});
            skLineSegment(sketch, "E34.11.19.0", {"start": v(-55.54, -88.88) * mm, "end": v(-61.71, -98.76) * mm});
            skArc(sketch, "E34.3.20.0", {"start": v(-42.63, -95.74) * mm, "mid": v(-39.26, -97.17) * mm, "end": v(-35.84, -98.48) * mm});
            skLineSegment(sketch, "E34.4.20.0", {"start": v(-39.83, -109.43) * mm, "end": v(-35.84, -98.48) * mm});
            skArc(sketch, "E34.7.20.0", {"start": v(-47.37, -106.39) * mm, "mid": v(-43.63, -107.98) * mm, "end": v(-39.83, -109.43) * mm});
            skLineSegment(sketch, "E34.11.20.0", {"start": v(-42.63, -95.74) * mm, "end": v(-47.37, -106.39) * mm});
            skArc(sketch, "E34.3.21.0", {"start": v(-28.89, -100.74) * mm, "mid": v(-25.35, -101.69) * mm, "end": v(-21.79, -102.51) * mm});
            skLineSegment(sketch, "E34.4.21.0", {"start": v(-24.21, -113.91) * mm, "end": v(-21.79, -102.51) * mm});
            skArc(sketch, "E34.7.21.0", {"start": v(-32.1, -111.95) * mm, "mid": v(-28.17, -113) * mm, "end": v(-24.21, -113.91) * mm});
            skLineSegment(sketch, "E34.11.21.0", {"start": v(-28.89, -100.74) * mm, "end": v(-32.1, -111.95) * mm});
            skArc(sketch, "E34.3.22.0", {"start": v(-14.59, -103.78) * mm, "mid": v(-10.95, -104.23) * mm, "end": v(-7.31, -104.55) * mm});
            skLineSegment(sketch, "E34.4.22.0", {"start": v(-8.12, -116.17) * mm, "end": v(-7.31, -104.55) * mm});
            skArc(sketch, "E34.7.22.0", {"start": v(-16.2, -115.32) * mm, "mid": v(-12.17, -115.82) * mm, "end": v(-8.12, -116.17) * mm});
            skLineSegment(sketch, "E34.11.22.0", {"start": v(-14.59, -103.78) * mm, "end": v(-16.2, -115.32) * mm});
            skArc(sketch, "E34.3.23.0", {"start": v(0, -104.8) * mm, "mid": v(3.66, -104.74) * mm, "end": v(7.31, -104.55) * mm});
            skLineSegment(sketch, "E34.4.23.0", {"start": v(8.12, -116.17) * mm, "end": v(7.31, -104.55) * mm});
            skArc(sketch, "E34.7.23.0", {"start": v(0, -116.46) * mm, "mid": v(4.06, -116.39) * mm, "end": v(8.12, -116.17) * mm});
            skLineSegment(sketch, "E34.11.23.0", {"start": v(0, -104.8) * mm, "end": v(0, -116.46) * mm});
            skArc(sketch, "E34.3.24.0", {"start": v(14.59, -103.78) * mm, "mid": v(18.2, -103.21) * mm, "end": v(21.79, -102.51) * mm});
            skLineSegment(sketch, "E34.4.24.0", {"start": v(24.21, -113.91) * mm, "end": v(21.79, -102.51) * mm});
            skArc(sketch, "E34.7.24.0", {"start": v(16.2, -115.32) * mm, "mid": v(20.22, -114.69) * mm, "end": v(24.21, -113.91) * mm});
            skLineSegment(sketch, "E34.11.24.0", {"start": v(14.59, -103.78) * mm, "end": v(16.2, -115.32) * mm});
            skArc(sketch, "E34.3.25.0", {"start": v(28.89, -100.74) * mm, "mid": v(32.39, -99.67) * mm, "end": v(35.84, -98.48) * mm});
            skLineSegment(sketch, "E34.4.25.0", {"start": v(39.83, -109.43) * mm, "end": v(35.84, -98.48) * mm});
            skArc(sketch, "E34.7.25.0", {"start": v(32.1, -111.95) * mm, "mid": v(35.99, -110.76) * mm, "end": v(39.83, -109.43) * mm});
            skLineSegment(sketch, "E34.11.25.0", {"start": v(28.89, -100.74) * mm, "end": v(32.1, -111.95) * mm});
            skArc(sketch, "E34.3.26.0", {"start": v(42.63, -95.74) * mm, "mid": v(45.94, -94.2) * mm, "end": v(49.2, -92.54) * mm});
            skLineSegment(sketch, "E34.4.26.0", {"start": v(54.67, -102.82) * mm, "end": v(49.2, -92.54) * mm});
            skArc(sketch, "E34.7.26.0", {"start": v(47.37, -106.39) * mm, "mid": v(51.05, -104.67) * mm, "end": v(54.67, -102.82) * mm});
            skLineSegment(sketch, "E34.11.26.0", {"start": v(42.63, -95.74) * mm, "end": v(47.37, -106.39) * mm});
            skArc(sketch, "E34.3.27.0", {"start": v(55.54, -88.88) * mm, "mid": v(58.6, -86.89) * mm, "end": v(61.6, -84.79) * mm});
            skLineSegment(sketch, "E34.4.27.0", {"start": v(68.45, -94.22) * mm, "end": v(61.6, -84.79) * mm});
            skArc(sketch, "E34.7.27.0", {"start": v(61.71, -98.76) * mm, "mid": v(65.12, -96.55) * mm, "end": v(68.45, -94.22) * mm});
            skLineSegment(sketch, "E34.11.27.0", {"start": v(55.54, -88.88) * mm, "end": v(61.71, -98.76) * mm});
            skArc(sketch, "E34.3.28.0", {"start": v(67.37, -80.28) * mm, "mid": v(70.13, -77.88) * mm, "end": v(72.8, -75.39) * mm});
            skLineSegment(sketch, "E34.4.28.0", {"start": v(80.9, -83.77) * mm, "end": v(72.8, -75.39) * mm});
            skArc(sketch, "E34.7.28.0", {"start": v(74.86, -89.21) * mm, "mid": v(77.92, -86.54) * mm, "end": v(80.9, -83.77) * mm});
            skLineSegment(sketch, "E34.11.28.0", {"start": v(67.37, -80.28) * mm, "end": v(74.86, -89.21) * mm});
            skArc(sketch, "E34.3.29.0", {"start": v(77.88, -70.13) * mm, "mid": v(80.28, -67.37) * mm, "end": v(82.59, -64.52) * mm});
            skLineSegment(sketch, "E34.4.29.0", {"start": v(91.77, -71.7) * mm, "end": v(82.59, -64.52) * mm});
            skArc(sketch, "E34.7.29.0", {"start": v(86.54, -77.92) * mm, "mid": v(89.21, -74.86) * mm, "end": v(91.77, -71.7) * mm});
            skLineSegment(sketch, "E34.11.29.0", {"start": v(77.88, -70.13) * mm, "end": v(86.54, -77.92) * mm});
            skArc(sketch, "E34.3.30.0", {"start": v(86.89, -58.6) * mm, "mid": v(88.88, -55.54) * mm, "end": v(90.76, -52.4) * mm});
            skLineSegment(sketch, "E34.4.30.0", {"start": v(100.85, -58.23) * mm, "end": v(90.76, -52.4) * mm});
            skArc(sketch, "E34.7.30.0", {"start": v(96.55, -65.12) * mm, "mid": v(98.76, -61.71) * mm, "end": v(100.85, -58.23) * mm});
            skLineSegment(sketch, "E34.11.30.0", {"start": v(86.89, -58.6) * mm, "end": v(96.55, -65.12) * mm});
            skArc(sketch, "E34.3.31.0", {"start": v(94.2, -45.94) * mm, "mid": v(95.74, -42.63) * mm, "end": v(97.17, -39.26) * mm});
            skLineSegment(sketch, "E34.4.31.0", {"start": v(107.98, -43.63) * mm, "end": v(97.17, -39.26) * mm});
            skArc(sketch, "E34.7.31.0", {"start": v(104.67, -51.05) * mm, "mid": v(106.39, -47.37) * mm, "end": v(107.98, -43.63) * mm});
            skLineSegment(sketch, "E34.11.31.0", {"start": v(94.2, -45.94) * mm, "end": v(104.67, -51.05) * mm});
            skArc(sketch, "E34.3.32.0", {"start": v(99.67, -32.39) * mm, "mid": v(100.74, -28.89) * mm, "end": v(101.69, -25.35) * mm});
            skLineSegment(sketch, "E34.4.32.0", {"start": v(113, -28.17) * mm, "end": v(101.69, -25.35) * mm});
            skArc(sketch, "E34.7.32.0", {"start": v(110.76, -35.99) * mm, "mid": v(111.95, -32.1) * mm, "end": v(113, -28.17) * mm});
            skLineSegment(sketch, "E34.11.32.0", {"start": v(99.67, -32.39) * mm, "end": v(110.76, -35.99) * mm});
            skArc(sketch, "E34.3.33.0", {"start": v(103.21, -18.2) * mm, "mid": v(103.78, -14.59) * mm, "end": v(104.23, -10.95) * mm});
            skLineSegment(sketch, "E34.4.33.0", {"start": v(115.82, -12.17) * mm, "end": v(104.23, -10.95) * mm});
            skArc(sketch, "E34.7.33.0", {"start": v(114.69, -20.22) * mm, "mid": v(115.32, -16.2) * mm, "end": v(115.82, -12.17) * mm});
            skLineSegment(sketch, "E34.11.33.0", {"start": v(103.21, -18.2) * mm, "end": v(114.69, -20.22) * mm});
            skArc(sketch, "E34.3.34.0", {"start": v(104.74, -3.66) * mm, "mid": v(104.8, 0) * mm, "end": v(104.74, 3.66) * mm});
            skLineSegment(sketch, "E34.4.34.0", {"start": v(116.39, 4.06) * mm, "end": v(104.74, 3.66) * mm});
            skArc(sketch, "E34.7.34.0", {"start": v(116.39, -4.06) * mm, "mid": v(116.46, 0) * mm, "end": v(116.39, 4.06) * mm});
            skLineSegment(sketch, "E34.11.34.0", {"start": v(104.74, -3.66) * mm, "end": v(116.39, -4.06) * mm});
            skArc(sketch, "E34.3.35.0", {"start": v(104.23, 10.95) * mm, "mid": v(103.78, 14.59) * mm, "end": v(103.21, 18.2) * mm});
            skLineSegment(sketch, "E34.4.35.0", {"start": v(114.69, 20.22) * mm, "end": v(103.21, 18.2) * mm});
            skArc(sketch, "E34.7.35.0", {"start": v(115.82, 12.17) * mm, "mid": v(115.32, 16.2) * mm, "end": v(114.69, 20.22) * mm});
            skLineSegment(sketch, "E34.11.35.0", {"start": v(104.23, 10.95) * mm, "end": v(115.82, 12.17) * mm});
            skArc(sketch, "E35.3.36.0", {"start": v(101.69, 25.35) * mm, "mid": v(100.74, 28.89) * mm, "end": v(99.67, 32.39) * mm});
            skLineSegment(sketch, "E35.4.36.0", {"start": v(110.76, 35.99) * mm, "end": v(99.67, 32.39) * mm});
            skArc(sketch, "E35.7.36.0", {"start": v(113, 28.17) * mm, "mid": v(111.95, 32.1) * mm, "end": v(110.76, 35.99) * mm});
            skLineSegment(sketch, "E35.11.36.0", {"start": v(101.69, 25.35) * mm, "end": v(113, 28.17) * mm});
            skArc(sketch, "E35.3.37.0", {"start": v(97.17, 39.26) * mm, "mid": v(95.74, 42.63) * mm, "end": v(94.2, 45.94) * mm});
            skLineSegment(sketch, "E35.4.37.0", {"start": v(104.67, 51.05) * mm, "end": v(94.2, 45.94) * mm});
            skArc(sketch, "E35.7.37.0", {"start": v(107.98, 43.63) * mm, "mid": v(106.39, 47.37) * mm, "end": v(104.67, 51.05) * mm});
            skLineSegment(sketch, "E35.11.37.0", {"start": v(97.17, 39.26) * mm, "end": v(107.98, 43.63) * mm});
            skArc(sketch, "E35.3.38.0", {"start": v(90.76, 52.4) * mm, "mid": v(88.88, 55.54) * mm, "end": v(86.89, 58.6) * mm});
            skLineSegment(sketch, "E35.4.38.0", {"start": v(96.55, 65.12) * mm, "end": v(86.89, 58.6) * mm});
            skArc(sketch, "E35.7.38.0", {"start": v(100.85, 58.23) * mm, "mid": v(98.76, 61.71) * mm, "end": v(96.55, 65.12) * mm});
            skLineSegment(sketch, "E35.11.38.0", {"start": v(90.76, 52.4) * mm, "end": v(100.85, 58.23) * mm});
            skArc(sketch, "E35.3.39.0", {"start": v(82.59, 64.52) * mm, "mid": v(80.28, 67.37) * mm, "end": v(77.88, 70.13) * mm});
            skLineSegment(sketch, "E35.4.39.0", {"start": v(86.54, 77.92) * mm, "end": v(77.88, 70.13) * mm});
            skArc(sketch, "E35.7.39.0", {"start": v(91.77, 71.7) * mm, "mid": v(89.21, 74.86) * mm, "end": v(86.54, 77.92) * mm});
            skLineSegment(sketch, "E35.11.39.0", {"start": v(82.59, 64.52) * mm, "end": v(91.77, 71.7) * mm});
            skArc(sketch, "E35.3.40.0", {"start": v(72.8, 75.39) * mm, "mid": v(70.13, 77.88) * mm, "end": v(67.37, 80.28) * mm});
            skLineSegment(sketch, "E35.4.40.0", {"start": v(74.86, 89.21) * mm, "end": v(67.37, 80.28) * mm});
            skArc(sketch, "E35.7.40.0", {"start": v(80.9, 83.77) * mm, "mid": v(77.92, 86.54) * mm, "end": v(74.86, 89.21) * mm});
            skLineSegment(sketch, "E35.11.40.0", {"start": v(72.8, 75.39) * mm, "end": v(80.9, 83.77) * mm});
            skArc(sketch, "E35.3.41.0", {"start": v(61.6, 84.79) * mm, "mid": v(58.6, 86.89) * mm, "end": v(55.54, 88.88) * mm});
            skLineSegment(sketch, "E35.4.41.0", {"start": v(61.71, 98.76) * mm, "end": v(55.54, 88.88) * mm});
            skArc(sketch, "E35.7.41.0", {"start": v(68.45, 94.22) * mm, "mid": v(65.12, 96.55) * mm, "end": v(61.71, 98.76) * mm});
            skLineSegment(sketch, "E35.11.41.0", {"start": v(61.6, 84.79) * mm, "end": v(68.45, 94.22) * mm});
            skArc(sketch, "E35.3.42.0", {"start": v(49.2, 92.54) * mm, "mid": v(45.94, 94.2) * mm, "end": v(42.63, 95.74) * mm});
            skLineSegment(sketch, "E35.4.42.0", {"start": v(47.37, 106.39) * mm, "end": v(42.63, 95.74) * mm});
            skArc(sketch, "E35.7.42.0", {"start": v(54.67, 102.82) * mm, "mid": v(51.05, 104.67) * mm, "end": v(47.37, 106.39) * mm});
            skLineSegment(sketch, "E35.11.42.0", {"start": v(49.2, 92.54) * mm, "end": v(54.67, 102.82) * mm});
            skArc(sketch, "E35.3.43.0", {"start": v(35.84, 98.48) * mm, "mid": v(32.39, 99.67) * mm, "end": v(28.89, 100.74) * mm});
            skLineSegment(sketch, "E35.4.43.0", {"start": v(32.1, 111.95) * mm, "end": v(28.89, 100.74) * mm});
            skArc(sketch, "E35.7.43.0", {"start": v(39.83, 109.43) * mm, "mid": v(35.99, 110.76) * mm, "end": v(32.1, 111.95) * mm});
            skLineSegment(sketch, "E35.11.43.0", {"start": v(35.84, 98.48) * mm, "end": v(39.83, 109.43) * mm});
            skArc(sketch, "E35.3.44.0", {"start": v(21.79, 102.51) * mm, "mid": v(18.2, 103.21) * mm, "end": v(14.59, 103.78) * mm});
            skLineSegment(sketch, "E35.4.44.0", {"start": v(16.2, 115.32) * mm, "end": v(14.59, 103.78) * mm});
            skArc(sketch, "E35.7.44.0", {"start": v(24.21, 113.91) * mm, "mid": v(20.22, 114.69) * mm, "end": v(16.2, 115.32) * mm});
            skLineSegment(sketch, "E35.11.44.0", {"start": v(21.79, 102.51) * mm, "end": v(24.21, 113.91) * mm});
            skSolve(sketch);
        }
        {
            var Q0;
            Q0=qSketchRegion(id+"F4",true);
            extrude(context, id + "F5", {"entities" : qUnion([Q0]), "operationType" : NewBodyOperationType.REMOVE, "oppositeDirection" : true, "depth" : 25 * mm, "offsetDistance" : 25 * mm});
        }
        {
            var Q0;
            Q0=makeQuery(id+"F3.boolean.opBoolean","MERGE",FACE,{"derivedFrom":[makeQuery(id+"F1.opExtrude","CAP_FACE",FACE,{"disambiguationData":[OSD([sQuery(id+"F0.wireOp",EDGE,"E6"),sQuery(id+"F0.wireOp",EDGE,"E7"),sQuery(id+"F0.wireOp",EDGE,"E8"),sQuery(id+"F0.wireOp",EDGE,"E9"),sQuery(id+"F0.wireOp",EDGE,"E10.MirrorCS"),sQuery(id+"F0.wireOp",EDGE,"E11.MirrorCS"),sQuery(id+"F0.wireOp",EDGE,"E12.MirrorCS"),sQuery(id+"F0.wireOp",EDGE,"E13.MirrorCS"),sQuery(id+"F0.wireOp",EDGE,"E14.MirrorCS"),sQuery(id+"F0.wireOp",EDGE,"E15.MirrorCS"),sQuery(id+"F0.wireOp",EDGE,"E16.MirrorCS"),sQuery(id+"F0.wireOp",EDGE,"E17.MirrorCS"),sQuery(id+"F0.wireOp",EDGE,"E18.MirrorCS"),sQuery(id+"F0.wireOp",EDGE,"E19.MirrorCS"),sQuery(id+"F0.wireOp",EDGE,"E20.MirrorCS"),sQuery(id+"F0.wireOp",EDGE,"E21.MirrorCS"),sQuery(id+"F0.wireOp",EDGE,"E25")])],"isStart":false}),makeQuery(id+"F3.opExtrude","CAP_FACE",FACE,{"disambiguationData":[OSD([sQuery(id+"F2.wireOp",EDGE,"E26"),sQuery(id+"F2.wireOp",EDGE,"E27")])],"isStart":true})]});
            var sketch = newSketch(context, id + "F6", { "sketchPlane" : qUnion([Q0])});
            skCircle(sketch, "E36", {"center": v(0, 0) * mm, "radius": 95 * mm});
            skSolve(sketch);
        }
        {
            var Q0;
            Q0 = qSketchRegion(id + "F6", true);
            extrude(context, id + "F7", {"entities" : qUnion([Q0]), "operationType" : NewBodyOperationType.REMOVE, "oppositeDirection" : true, "depth" : 25 * mm, "offsetDistance" : 25 * mm});
        }
    });
